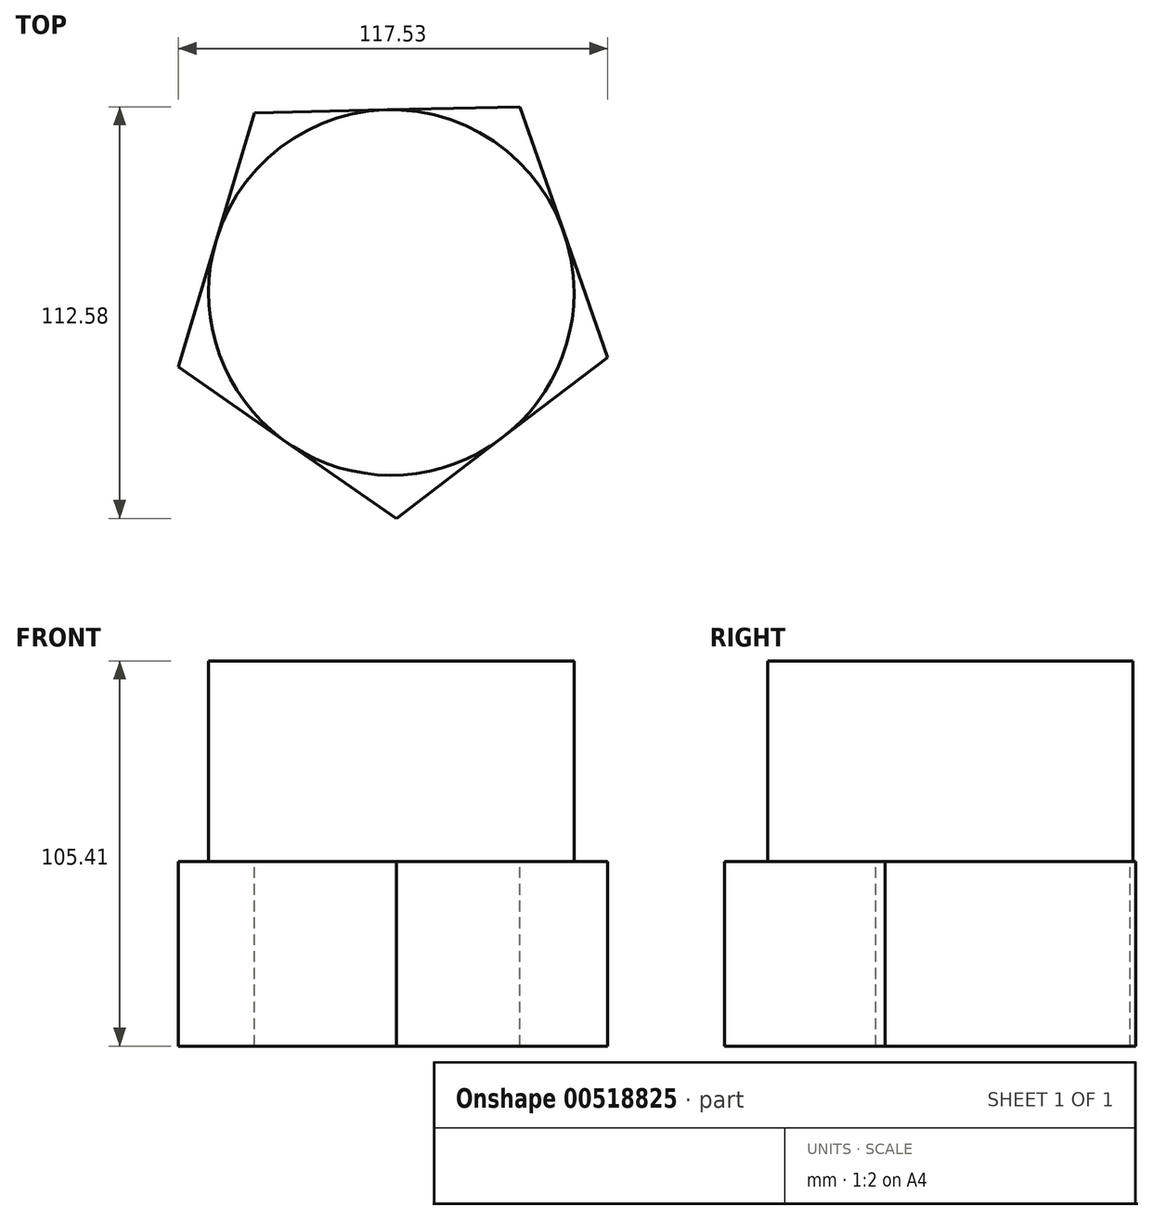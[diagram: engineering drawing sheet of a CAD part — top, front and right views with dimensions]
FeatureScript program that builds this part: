
annotation { "Feature Type Name" : "Feature", "Feature Type Description" : "" }
export const myFeature = defineFeature(function(context is Context, id is Id, definition is map)
    precondition{}
    {
        {
            var Q0;
            Q0=qCreatedBy(makeId("Top.planeOp"),FACE);
            var sketch = newSketch(context, id + "F0", { "sketchPlane" : qUnion([Q0])});
            skCircle(sketch, "E0", {"center": v(0, 0) * mm, "radius": 50 * mm});
            skSolve(sketch);
        }
        {
            var Q0;
            Q0 = qSketchRegion(id + "F0", true);
            extrude(context, id + "F1", {"entities" : qUnion([Q0]), "depth" : 54.86 * mm, "offsetDistance" : 25.4 * mm});
        }
        {
            var Q0;
            Q0=makeQuery(id+"F1.opExtrude","CAP_FACE",FACE,{"disambiguationData":[OSD([sQuery(id+"F0.wireOp",EDGE,"E0")])],"isStart":true});
            var sketch = newSketch(context, id + "F2", { "sketchPlane" : qUnion([Q0])});
            skCircle(sketch, "E1.cCircle", {"center": v(0, 0) * mm, "radius": 50 * mm, "construction": true});
            skLineSegment(sketch, "E1.0", {"start": v(1.36, 61.79) * mm, "end": v(59.18, 17.8) * mm});
            skLineSegment(sketch, "E1.1", {"start": v(59.18, 17.8) * mm, "end": v(35.22, -50.79) * mm});
            skLineSegment(sketch, "E1.2", {"start": v(35.22, -50.79) * mm, "end": v(-37.42, -49.2) * mm});
            skLineSegment(sketch, "E1.3", {"start": v(-37.42, -49.2) * mm, "end": v(-58.35, 20.38) * mm});
            skLineSegment(sketch, "E1.4", {"start": v(-58.35, 20.38) * mm, "end": v(1.36, 61.79) * mm});
            skPoint(sketch, "E1.0.midPoint", {"position": v(30.27, 39.8) * mm});
            skSolve(sketch);
        }
        {
            var Q0;
            {var subQ0=sQuery(id+"F2.wireOp",EDGE,"E1.4");var subQ1=sQuery(id+"F2.wireOp",EDGE,"E1.3");var subQ2=makeQuery(id+"F2.imprint","INTERSECT",VERTEX,{"derivedFrom":[subQ1,subQ0]});Q0=makeQuery(id+"F2.imprint","IMPRINT",FACE,{"disambiguationData":[TD([[makeQuery(id+"F2.imprint","IMPRINT",EDGE,{"disambiguationData":[TD([[subQ2,1.0]])],"derivedFrom":subQ1}),-1.0]])]});}
            var Q1;
            {var subQ0=sQuery(id+"F2.wireOp",EDGE,"E1.3");var subQ1=sQuery(id+"F2.wireOp",EDGE,"E1.2");var subQ2=makeQuery(id+"F2.imprint","INTERSECT",VERTEX,{"derivedFrom":[subQ1,subQ0]});Q1=makeQuery(id+"F2.imprint","IMPRINT",FACE,{"disambiguationData":[TD([[makeQuery(id+"F2.imprint","IMPRINT",EDGE,{"disambiguationData":[TD([[subQ2,1.0]])],"derivedFrom":subQ1}),-1.0]])]});}
            var Q2;
            {var subQ0=sQuery(id+"F2.wireOp",EDGE,"E1.2");var subQ1=sQuery(id+"F2.wireOp",EDGE,"E1.1");var subQ2=makeQuery(id+"F2.imprint","INTERSECT",VERTEX,{"derivedFrom":[subQ1,subQ0]});Q2=makeQuery(id+"F2.imprint","IMPRINT",FACE,{"disambiguationData":[TD([[makeQuery(id+"F2.imprint","IMPRINT",EDGE,{"disambiguationData":[TD([[subQ2,1.0]])],"derivedFrom":subQ1}),-1.0]])]});}
            var Q3;
            {var subQ0=sQuery(id+"F2.wireOp",EDGE,"E1.1");var subQ1=sQuery(id+"F2.wireOp",EDGE,"E1.0");var subQ2=makeQuery(id+"F2.imprint","INTERSECT",VERTEX,{"derivedFrom":[subQ1,subQ0]});Q3=makeQuery(id+"F2.imprint","IMPRINT",FACE,{"disambiguationData":[TD([[makeQuery(id+"F2.imprint","IMPRINT",EDGE,{"disambiguationData":[TD([[subQ2,1.0]])],"derivedFrom":subQ1}),-1.0]])]});}
            var Q4;
            {var subQ0=sQuery(id+"F2.wireOp",EDGE,"E1.4");var subQ1=sQuery(id+"F2.wireOp",EDGE,"E1.0");var subQ2=makeQuery(id+"F2.imprint","INTERSECT",VERTEX,{"derivedFrom":[subQ1,subQ0]});Q4=makeQuery(id+"F2.imprint","IMPRINT",FACE,{"disambiguationData":[TD([[makeQuery(id+"F2.imprint","IMPRINT",EDGE,{"disambiguationData":[TD([[subQ2,-1.0]])],"derivedFrom":subQ1}),-1.0]])]});}
            var Q5;
            {var subQ0=makeQuery(id+"F1.opExtrude","CAP_EDGE",EDGE,{"disambiguationData":[OSD([sQuery(id+"F0.wireOp",EDGE,"E0")])],"isStart":true});var subQ4=makeQuery(id+"F2.imprint","INTERSECT",VERTEX,{"derivedFrom":[subQ0,sQuery(id+"F2.wireOp",EDGE,"E1.0")]});Q5=makeQuery(id+"F2.imprint","IMPRINT",FACE,{"disambiguationData":[TD([[makeQuery(id+"F2.imprint","IMPRINT",EDGE,{"disambiguationData":[TD([[subQ4,-1.0]])],"derivedFrom":subQ0}),-1.0]])]});}
            extrude(context, id + "F3", {"entities" : qUnion([Q0, Q1, Q2, Q3, Q4, Q5]), "operationType" : NewBodyOperationType.ADD, "depth" : 50.55 * mm, "offsetDistance" : 25.4 * mm});
        }
    });
